# Revit family: M_Check Valve_Fitting
name_source: partatom
category: Pipe Accessories
revit_build: Autodesk Revit 2017 (Build: 20171027_0315(x64)
units: mm (PartAtom-declared; Revit-internal decimal feet)

## family parameters
Always vertical = Yes
Cut with Voids When Loaded = No
OmniClass Number = 23.65.55.14.21
OmniClass Title = Non-Return Valves for Liquid Services
Part Type = Valve - Breaks Into
Round Connector Dimension = Use Radius
Shared = No
Work Plane-Based = No

## types (10) — shared parameters
Valve Material = <By Category>

## per-type parameters (varying)
| type | Adapter Diameter | Adapter Length | Adapter Radius | Body Diameter | Body Length | Body Radius | Cover Diameter | Cover Height | Cover Radius | Cover Thickness | Height 1 | K Coefficient | Length 1 | Length 2 | Nominal Radius | Width 1 |
| 100 mm | 120 mm | 18 mm  [stored 0.0590551 ft] | 60 mm | 72 mm | 184 mm | 36 mm  [stored 0.11811 ft] | 120 mm | 114 mm | 60 mm | 28 mm | 32 mm | 0.21 | 12 mm  [stored 0.0393701 ft] | 27 mm | 50 mm | 7 mm  [stored 0.0229659 ft] |
| 10 mm | 12 mm  [stored 0.0393701 ft] | 5 mm  [stored 0.0164042 ft] | 6 mm  [stored 0.019685 ft] | 7 mm  [stored 0.0229659 ft] | 52 mm | 4 mm  [stored 0.0131234 ft] | 34 mm | 38 mm  [stored 0.124672 ft] | 17 mm | 8 mm  [stored 0.0262467 ft] | 6 mm  [stored 0.019685 ft] | 0.35 | 1 mm  [stored 0.00328084 ft] | 8 mm  [stored 0.0262467 ft] | 5 mm | 2 mm  [stored 0.00656168 ft] |
| 20 mm | 24 mm  [stored 0.0787402 ft] | 6 mm  [stored 0.019685 ft] | 12 mm  [stored 0.0393701 ft] | 14 mm  [stored 0.0459318 ft] | 60 mm | 7 mm  [stored 0.0229659 ft] | 39 mm  [stored 0.127953 ft] | 43 mm | 20 mm | 9 mm  [stored 0.0295276 ft] | 6 mm  [stored 0.019685 ft] | 0.32 | 2 mm  [stored 0.00656168 ft] | 9 mm  [stored 0.0295276 ft] | 10 mm | 2 mm  [stored 0.00656168 ft] |
| 80 mm | 96 mm | 15 mm | 48 mm | 58 mm | 149 mm | 29 mm | 97 mm | 95 mm | 48 mm | 22 mm | 25 mm  [stored 0.082021 ft] | 0.32 | 10 mm  [stored 0.0328084 ft] | 22 mm | 40 mm | 5 mm  [stored 0.0164042 ft] |
| 50 mm | 60 mm | 11 mm | 30 mm | 36 mm  [stored 0.11811 ft] | 108 mm | 18 mm  [stored 0.0590551 ft] | 70 mm | 73 mm | 35 mm | 16 mm | 19 mm | 0.25 | 6 mm  [stored 0.019685 ft] | 16 mm | 25 mm | 4 mm  [stored 0.0131234 ft] |
| 65 mm | 78 mm | 14 mm  [stored 0.0459318 ft] | 39 mm  [stored 0.127953 ft] | 47 mm | 140 mm | 23 mm | 91 mm | 89 mm | 46 mm | 21 mm | 19 mm | 0.24 | 8 mm  [stored 0.0262467 ft] | 20 mm | 33 mm | 5 mm  [stored 0.0164042 ft] |
| 15 mm | 18 mm  [stored 0.0590551 ft] | 6 mm  [stored 0.019685 ft] | 9 mm  [stored 0.0295276 ft] | 11 mm | 57 mm | 5 mm  [stored 0.0164042 ft] | 37 mm | 38 mm  [stored 0.124672 ft] | 19 mm | 9 mm  [stored 0.0295276 ft] | 6 mm  [stored 0.019685 ft] | 0.32 | 2 mm  [stored 0.00656168 ft] | 8 mm  [stored 0.0262467 ft] | 8 mm | 2 mm  [stored 0.00656168 ft] |
| 25 mm | 30 mm | 7 mm  [stored 0.0229659 ft] | 15 mm | 18 mm  [stored 0.0590551 ft] | 70 mm | 9 mm  [stored 0.0295276 ft] | 46 mm | 49 mm | 23 mm | 11 mm | 13 mm | 0.31 | 3 mm  [stored 0.00984252 ft] | 10 mm  [stored 0.0328084 ft] | 13 mm | 3 mm  [stored 0.00984252 ft] |
| 32 mm | 38 mm  [stored 0.124672 ft] | 8 mm  [stored 0.0262467 ft] | 19 mm | 23 mm | 83 mm | 12 mm  [stored 0.0393701 ft] | 54 mm | 56 mm | 27 mm | 12 mm  [stored 0.0393701 ft] | 13 mm | 0.3 | 4 mm  [stored 0.0131234 ft] | 12 mm  [stored 0.0393701 ft] | 16 mm | 3 mm  [stored 0.00984252 ft] |
| 40 mm | 48 mm | 9 mm  [stored 0.0295276 ft] | 24 mm  [stored 0.0787402 ft] | 29 mm | 92 mm | 14 mm  [stored 0.0459318 ft] | 60 mm | 59 mm | 30 mm | 14 mm  [stored 0.0459318 ft] | 13 mm | 0.28 | 5 mm  [stored 0.0164042 ft] | 13 mm | 20 mm | 3 mm  [stored 0.00984252 ft] |

note: column(s) folded — value = type name in every type: Nominal Diameter

note: [stored X ft] marks values corroborated as IEEE doubles in the binary element streams (Revit-internal decimal feet)
